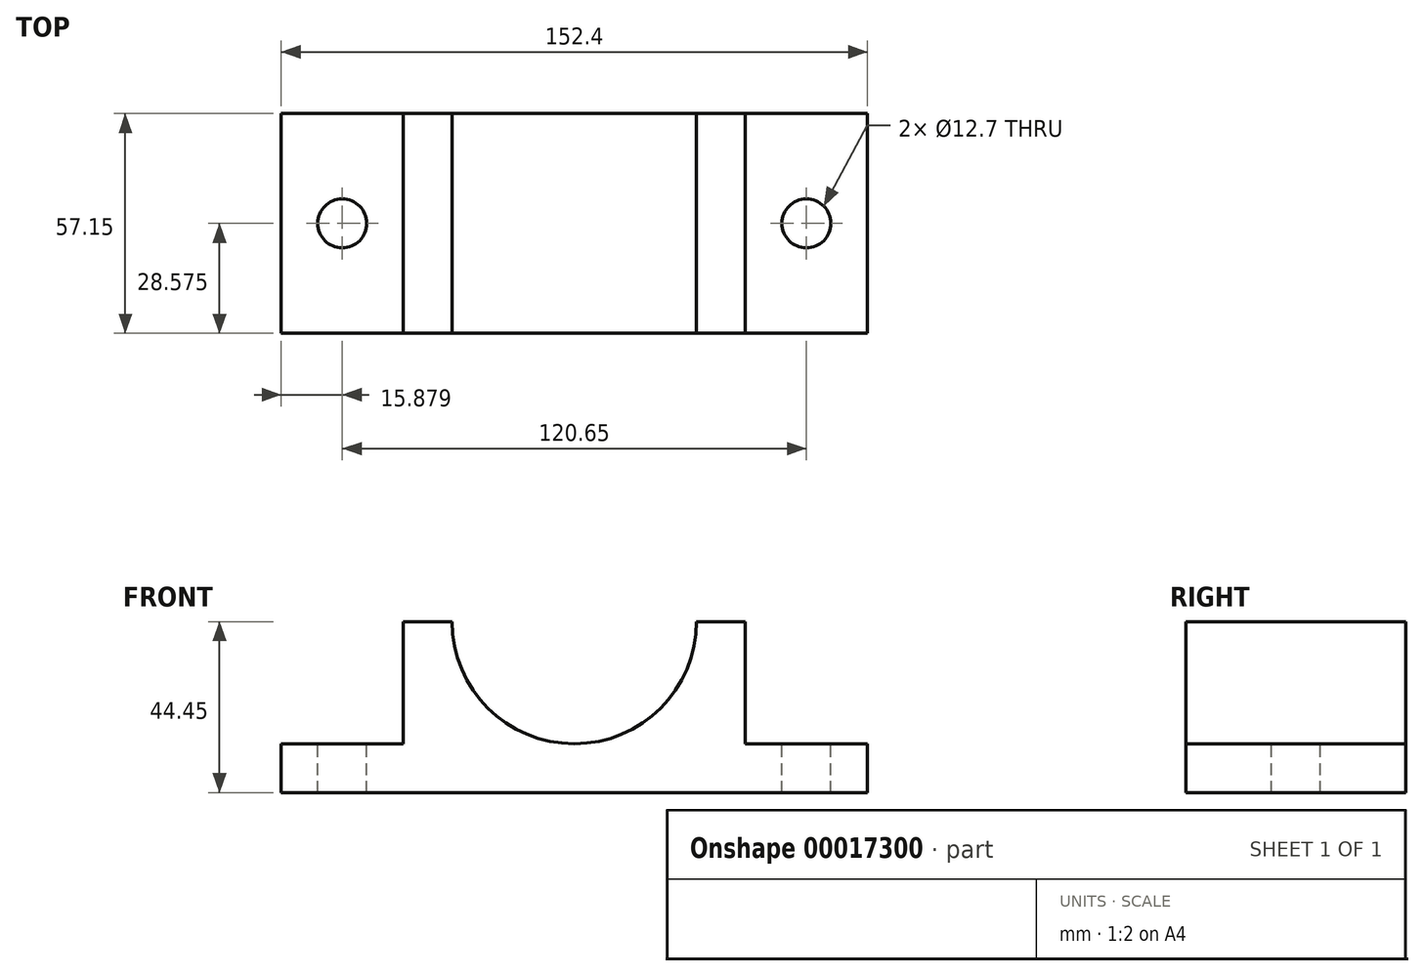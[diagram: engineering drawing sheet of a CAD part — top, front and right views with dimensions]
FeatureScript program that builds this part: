
annotation { "Feature Type Name" : "Feature", "Feature Type Description" : "" }
export const myFeature = defineFeature(function(context is Context, id is Id, definition is map)
    precondition{}
    {
        {
            var Q0;
            Q0=qCreatedBy(makeId("Front.planeOp"),FACE);
            var sketch = newSketch(context, id + "F0", { "sketchPlane" : qUnion([Q0])});
            skLineSegment(sketch, "E0", {"start": v(-70.72, 0) * mm, "end": v(-70.72, -12.7) * mm});
            skLineSegment(sketch, "E1", {"start": v(-70.72, -12.7) * mm, "end": v(81.68, -12.7) * mm});
            skLineSegment(sketch, "E2", {"start": v(81.68, -12.7) * mm, "end": v(81.68, 0) * mm});
            skLineSegment(sketch, "E3", {"start": v(-70.72, 0) * mm, "end": v(-38.97, 0) * mm});
            skLineSegment(sketch, "E4", {"start": v(81.68, 0) * mm, "end": v(49.93, 0) * mm});
            skLineSegment(sketch, "E5", {"start": v(-38.97, 0) * mm, "end": v(-38.97, 31.75) * mm});
            skLineSegment(sketch, "E6", {"start": v(49.93, 31.75) * mm, "end": v(49.93, 0) * mm});
            skLineSegment(sketch, "E7", {"start": v(-38.97, 31.75) * mm, "end": v(-26.27, 31.75) * mm});
            skLineSegment(sketch, "E8", {"start": v(49.93, 31.75) * mm, "end": v(37.23, 31.75) * mm});
            skArc(sketch, "E9", {"start": v(-26.27, 31.75) * mm, "mid": v(5.48, 0) * mm, "end": v(37.23, 31.75) * mm});
            skSolve(sketch);
        }
        {
            var Q0;
            Q0 = qSketchRegion(id + "F0", true);
            extrude(context, id + "F1", {"entities" : qUnion([Q0]), "depth" : 57.15 * mm});
        }
        {
            var Q0;
            Q0=makeQuery(id+"F1.opExtrude","SWEPT_FACE",FACE,{"disambiguationData":[OSD([sQuery(id+"F0.wireOp",EDGE,"E4")])]});
            var sketch = newSketch(context, id + "F2", { "sketchPlane" : qUnion([Q0])});
            skCircle(sketch, "E10", {"center": v(65.8, -28.58) * mm, "radius": 6.35 * mm});
            skSolve(sketch);
        }
        {
            var Q0;
            Q0=makeQuery(id+"F1.opExtrude","SWEPT_FACE",FACE,{"disambiguationData":[OSD([sQuery(id+"F0.wireOp",EDGE,"E3")])]});
            var sketch = newSketch(context, id + "F3", { "sketchPlane" : qUnion([Q0])});
            skCircle(sketch, "E11", {"center": v(-54.84, -28.58) * mm, "radius": 6.35 * mm});
            skSolve(sketch);
        }
        {
            var Q0;
            Q0=makeQuery(id+"F2.imprint","IMPRINT",FACE,{"disambiguationData":[TD([[makeQuery(id+"F2.imprint","IMPRINT",EDGE,{"derivedFrom":sQuery(id+"F2.wireOp",EDGE,"E10")}),1.0]])]});
            extrude(context, id + "F4", {"entities" : qUnion([Q0]), "operationType" : NewBodyOperationType.REMOVE, "endBound" : BoundingType.THROUGH_ALL, "oppositeDirection" : true, "depth" : 25.4 * mm});
        }
        {
            var Q0;
            Q0=makeQuery(id+"F3.imprint","IMPRINT",FACE,{"disambiguationData":[TD([[makeQuery(id+"F3.imprint","IMPRINT",EDGE,{"derivedFrom":sQuery(id+"F3.wireOp",EDGE,"E11")}),1.0]])]});
            extrude(context, id + "F5", {"entities" : qUnion([Q0]), "operationType" : NewBodyOperationType.REMOVE, "endBound" : BoundingType.THROUGH_ALL, "oppositeDirection" : true, "depth" : 25.4 * mm});
        }
    });
